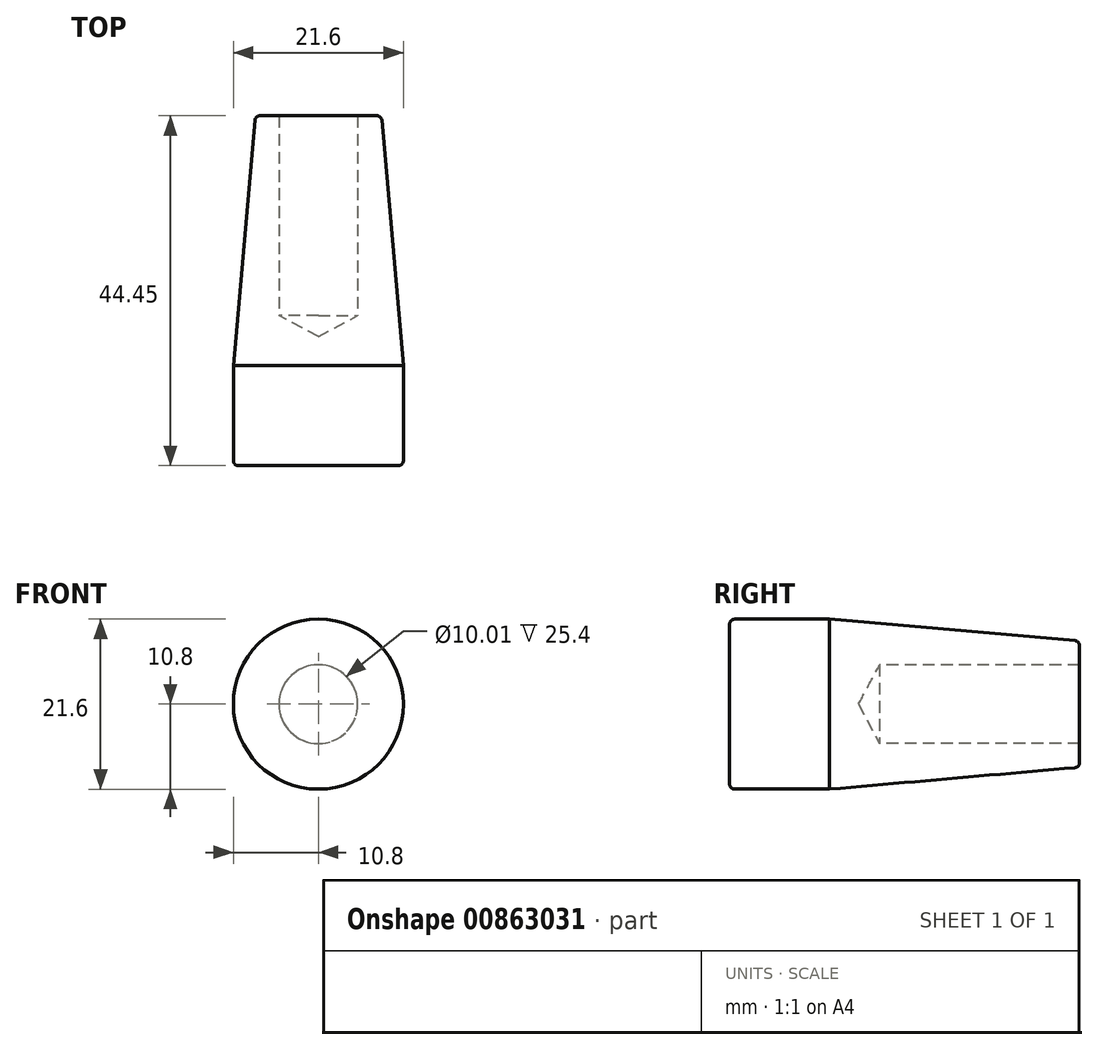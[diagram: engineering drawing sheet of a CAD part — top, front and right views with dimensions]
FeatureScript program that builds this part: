
annotation { "Feature Type Name" : "Feature", "Feature Type Description" : "" }
export const myFeature = defineFeature(function(context is Context, id is Id, definition is map)
    precondition{}
    {
        {
            var Q0;
            Q0=qCreatedBy(makeId("Right.planeOp"),FACE);
            var sketch = newSketch(context, id + "F0", { "sketchPlane" : qUnion([Q0])});
            skLineSegment(sketch, "E0", {"start": v(0, 5) * mm, "end": v(0, 7.44) * mm});
            skLineSegment(sketch, "E1", {"start": v(-0.58, 8.07) * mm, "end": v(-31.75, 10.8) * mm});
            skLineSegment(sketch, "E2", {"start": v(-31.75, 10.8) * mm, "end": v(-43.82, 10.8) * mm});
            skLineSegment(sketch, "E3", {"start": v(-44.45, 10.16) * mm, "end": v(-44.45, 0) * mm});
            skLineSegment(sketch, "E4", {"start": v(-44.45, 0) * mm, "end": v(-28.06, 0) * mm});
            skLineSegment(sketch, "E5", {"start": v(0, 5) * mm, "end": v(-25.4, 5) * mm});
            skLineSegment(sketch, "E6", {"start": v(-25.4, 5) * mm, "end": v(-28.06, 0) * mm});
            skPoint(sketch, "E7.orphan", {"position": v(0, 0) * mm});
            skPoint(sketch, "E8.visualSharp", {"position": v(-44.45, 10.8) * mm});
            skArc(sketch, "E8.filletArc", {"start": v(-43.82, 10.8) * mm, "mid": v(-44.26, 10.6) * mm, "end": v(-44.45, 10.16) * mm});
            skPoint(sketch, "E9.visualSharp", {"position": v(0, 8.02) * mm});
            skArc(sketch, "E9.filletArc", {"start": v(0, 7.44) * mm, "mid": v(-0.17, 7.86) * mm, "end": v(-0.58, 8.07) * mm});
            skSolve(sketch);
        }
        {
            var Q0;
            Q0 = qSketchRegion(id + "F0", true);
            var Q1;
            Q1=sQuery(id+"F0.wireOp",EDGE,"E4");
            revolve(context, id + "F1", {"surfaceOperationType" : NewSurfaceOperationType.NEW, "entities" : qUnion([Q0]), "axis" : qUnion([Q1]), "revolveType" : RevolveType.FULL});
        }
    });
